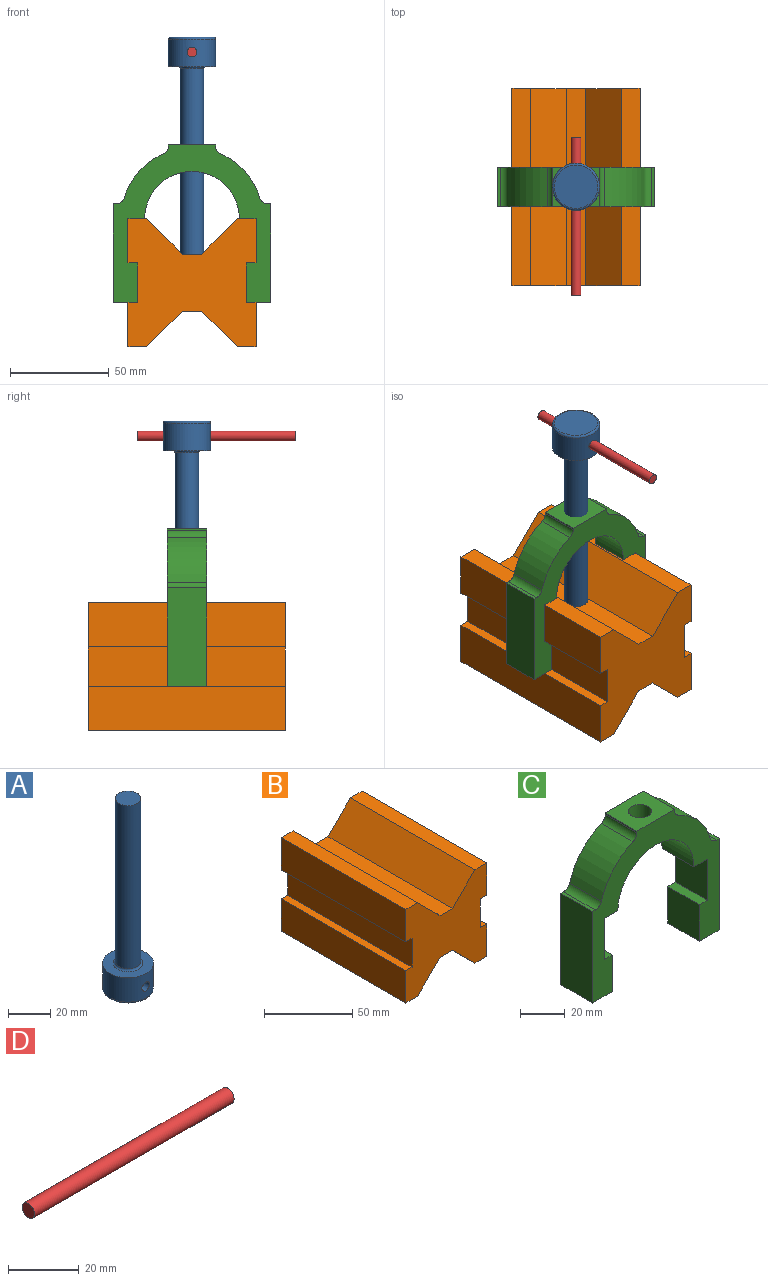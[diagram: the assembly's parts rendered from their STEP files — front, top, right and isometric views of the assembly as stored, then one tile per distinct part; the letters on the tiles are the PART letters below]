
ASSEMBLY  parts=4 mates=3
PART A: 8 faces, bbox 26x26x110 mm
  f0: cylinder r=12mm len=24mm, axis (0,0,-1), area 1015.9mm2, adj f1,f6,f7
  f1: plane 24x24mm, normal (0,0,1), area 298.5mm2, adj f0,f5
  f2: plane 22x22mm, normal (0,0,-1), area 380.1mm2, adj f6
  f3: cylinder r=6mm len=94mm, axis (0,0,-1), area 3543.7mm2, adj f4,f5
  f4: plane 12x12mm, normal (0,0,1), area 113.1mm2, adj f3
  f5: torus R=7mm, axis (0,0,1), area 62.8mm2, adj f1,f3
  f6: torus R=11mm, axis (0,0,1), area 114.8mm2, adj f0,f2
  f7: cylinder r=2.5mm len=24mm, axis (0,-1,0), area 372.9mm2, adj f0
PART B: 22 faces, bbox 65x100x65 mm
  f0: plane 100x10mm, normal (0,0,-1), area 1000mm2, adj f1,f19,f20,f21
  f1: plane 100x18mm, normal (-0.71,0,-0.71), area 2545.6mm2, adj f0,f2,f20,f21
  f2: plane 100x9.5mm, normal (0,0,-1), area 950mm2, adj f1,f3,f20,f21
  f3: plane 100x22.5mm, normal (1,0,0), area 2250mm2, adj f2,f4,f20,f21
  f4: plane 100x5mm, normal (0,0,1), area 500mm2, adj f3,f5,f20,f21
  f5: plane 100x20mm, normal (1,0,0), area 2000mm2, adj f4,f6,f20,f21
  f6: plane 100x5mm, normal (0,0,-1), area 500mm2, adj f5,f7,f20,f21
  f7: plane 100x22.5mm, normal (1,0,0), area 2250mm2, adj f6,f8,f20,f21
  f8: plane 100x9.5mm, normal (0,0,1), area 950mm2, adj f7,f9,f20,f21
  f9: plane 100x18mm, normal (-0.71,0,0.71), area 2545.6mm2, adj f8,f10,f20,f21
  f10: plane 100x10mm, normal (0,0,1), area 1000mm2, adj f9,f11,f20,f21
  f11: plane 100x18mm, normal (0.71,0,0.71), area 2545.6mm2, adj f10,f12,f20,f21
  f12: plane 100x9.5mm, normal (0,0,1), area 950mm2, adj f11,f13,f20,f21
  f13: plane 100x22.5mm, normal (-1,0,0), area 2250mm2, adj f12,f14,f20,f21
  f14: plane 100x5mm, normal (0,0,-1), area 500mm2, adj f13,f15,f20,f21
  f15: plane 100x20mm, normal (-1,0,0), area 2000mm2, adj f14,f16,f20,f21
  f16: plane 100x5mm, normal (0,0,1), area 500mm2, adj f15,f17,f20,f21
  f17: plane 100x22.5mm, normal (-1,0,0), area 2250mm2, adj f16,f18,f20,f21
  f18: plane 100x9.5mm, normal (0,0,-1), area 950mm2, adj f17,f19,f20,f21
  f19: plane 100x18mm, normal (0.71,0,-0.71), area 2545.6mm2, adj f0,f18,f20,f21
  f20: plane 65x65mm, normal (0,-1,0), area 3017mm2, adj f0,f1,f2,f3,f4,f5,f6,f7
  f21: plane 65x65mm, normal (0,1,0), area 3017mm2, adj f0,f1,f2,f3,f4,f5,f6,f7
PART C: 27 faces, bbox 80x20x80 mm
  f0: cylinder r=24mm len=48mm, axis (0,1,0), area 1424mm2, adj f16,f17,f24,f25,f26
  f1: cylinder r=4mm len=20mm, axis (0,1,0), area 102.3mm2, adj f2,f23,f24,f25
  f2: cylinder r=36mm len=22.64mm, axis (0,1,0), area 624.7mm2, adj f1,f3,f24,f25
  f3: cylinder r=4mm len=20mm, axis (0,1,0), area 92.7mm2, adj f2,f4,f24,f25
  f4: plane 20x0.84mm, normal (1,0,0), area 16.8mm2, adj f3,f5,f24,f25
  f5: plane 24x20mm, normal (0,0,1), area 396.7mm2, adj f4,f6,f24,f25,f26
  f6: plane 20x0.84mm, normal (-1,0,0), area 16.8mm2, adj f5,f7,f24,f25
  f7: cylinder r=4mm len=20mm, axis (0,1,0), area 92.7mm2, adj f6,f8,f24,f25
  f8: cylinder r=36mm len=22.64mm, axis (0,1,0), area 624.7mm2, adj f7,f9,f24,f25
  f9: cylinder r=4mm len=20mm, axis (0,1,0), area 102.3mm2, adj f8,f10,f24,f25
  f10: plane 20x1.69mm, normal (0,0,1), area 33.8mm2, adj f9,f11,f24,f25
  f11: plane 50x20mm, normal (-1,0,0), area 1000mm2, adj f10,f12,f24,f25
  f12: plane 20x12.5mm, normal (0,0,-1), area 250mm2, adj f11,f13,f24,f25
  f13: plane 20x20mm, normal (1,0,0), area 400mm2, adj f12,f14,f24,f25
  f14: plane 20x5mm, normal (0,0,1), area 100mm2, adj f13,f15,f24,f25
  f15: plane 22.5x20mm, normal (1,0,0), area 450mm2, adj f14,f16,f24,f25
  f16: plane 20x8.5mm, normal (0,0,-1), area 170mm2, adj f0,f15,f24,f25
  f17: plane 20x8.5mm, normal (0,0,-1), area 170mm2, adj f0,f18,f24,f25
  f18: plane 22.5x20mm, normal (-1,0,0), area 450mm2, adj f17,f19,f24,f25
  f19: plane 20x5mm, normal (0,0,1), area 100mm2, adj f18,f20,f24,f25
  f20: plane 20x20mm, normal (-1,0,0), area 400mm2, adj f19,f21,f24,f25
  f21: plane 20x12.5mm, normal (0,0,-1), area 250mm2, adj f20,f22,f24,f25
  f22: plane 50x20mm, normal (1,0,0), area 1000mm2, adj f21,f23,f24,f25
  f23: plane 20x1.69mm, normal (0,0,1), area 33.8mm2, adj f1,f22,f24,f25
  f24: plane 80x80mm, normal (0,-1,0), area 2090.8mm2, adj f0,f1,f2,f3,f4,f5,f6,f7
  f25: plane 80x80mm, normal (0,1,0), area 2090.8mm2, adj f0,f1,f2,f3,f4,f5,f6,f7
  f26: cylinder r=5.15mm len=14.06mm, axis (0,0,-1), area 445.9mm2, adj f0,f5
PART D: 3 faces, bbox 80x5x5 mm
  f0: cylinder r=2.5mm len=80mm, axis (-1,0,0), area 1256.6mm2, adj f1,f2
  f1: plane 5x5mm, normal (1,0,0), area 19.6mm2, adj f0
  f2: plane 5x5mm, normal (-1,0,0), area 19.6mm2, adj f0
PLACE A rot(axis=(1,0,0),180deg) t=(38.22,-20.83,226.84)mm
PLACE B t=(38.22,29.17,102.34)mm
PLACE C t=(38.22,-20.83,134.84)mm
PLACE D rot(axis=(-0.58,0.58,-0.58),120deg) t=(38.22,4,219.34)mm
MATE slider A.f7 <-> D.f0  axis (0,1,0) through (38.22,-20.83,219.34)mm
MATE fastened A.f0 <-> B.f10  axis (0,0,-1) through (38.22,-20.83,116.84)mm
MATE fastened B.f13 <-> C.f15  axis (-1,0,0) through (5.72,-20.83,123.59)mm
